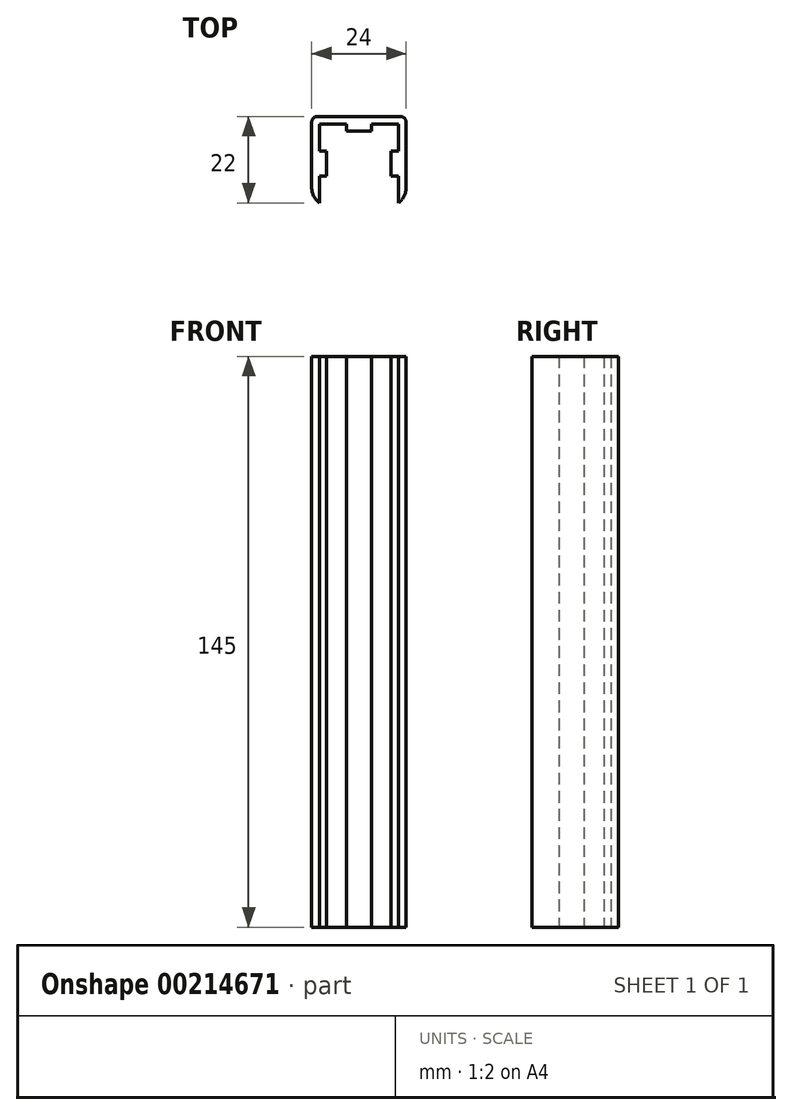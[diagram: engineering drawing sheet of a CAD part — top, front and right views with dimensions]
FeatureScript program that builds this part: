
annotation { "Feature Type Name" : "Feature", "Feature Type Description" : "" }
export const myFeature = defineFeature(function(context is Context, id is Id, definition is map)
    precondition{}
    {
        {
            var Q0;
            Q0=qCreatedBy(makeId("Top.planeOp"),FACE);
            var sketch = newSketch(context, id + "F0", { "sketchPlane" : qUnion([Q0])});
            skLineSegment(sketch, "E0", {"start": v(10.43, -32.44) * mm, "end": v(10.43, -25.64) * mm});
            skLineSegment(sketch, "E1", {"start": v(10.43, -25.64) * mm, "end": v(12.23, -25.64) * mm});
            skLineSegment(sketch, "E2", {"start": v(12.23, -25.64) * mm, "end": v(12.23, -19.24) * mm});
            skLineSegment(sketch, "E3", {"start": v(12.23, -19.24) * mm, "end": v(10.43, -19.24) * mm});
            skLineSegment(sketch, "E4", {"start": v(10.43, -19.24) * mm, "end": v(10.43, -12.44) * mm});
            skLineSegment(sketch, "E5", {"start": v(10.43, -12.44) * mm, "end": v(17.23, -12.44) * mm});
            skLineSegment(sketch, "E6", {"start": v(17.23, -12.44) * mm, "end": v(17.23, -14.24) * mm});
            skLineSegment(sketch, "E7", {"start": v(17.23, -14.24) * mm, "end": v(23.63, -14.24) * mm});
            skLineSegment(sketch, "E8", {"start": v(23.63, -14.24) * mm, "end": v(23.63, -12.44) * mm});
            skLineSegment(sketch, "E9", {"start": v(23.63, -12.44) * mm, "end": v(30.43, -12.44) * mm});
            skLineSegment(sketch, "E10", {"start": v(30.43, -12.44) * mm, "end": v(30.43, -19.24) * mm});
            skLineSegment(sketch, "E11", {"start": v(30.43, -19.24) * mm, "end": v(28.63, -19.24) * mm});
            skLineSegment(sketch, "E12", {"start": v(28.63, -19.24) * mm, "end": v(28.63, -25.64) * mm});
            skLineSegment(sketch, "E13", {"start": v(28.63, -25.64) * mm, "end": v(30.43, -25.64) * mm});
            skLineSegment(sketch, "E14", {"start": v(30.43, -25.64) * mm, "end": v(30.43, -32.44) * mm});
            skLineSegment(sketch, "E15", {"start": v(30.43, -32.44) * mm, "end": v(32.43, -32.44) * mm});
            skLineSegment(sketch, "E16", {"start": v(32.43, -32.44) * mm, "end": v(32.43, -10.44) * mm});
            skLineSegment(sketch, "E17", {"start": v(32.43, -10.44) * mm, "end": v(8.43, -10.44) * mm});
            skLineSegment(sketch, "E18", {"start": v(8.43, -10.44) * mm, "end": v(8.43, -32.44) * mm});
            skLineSegment(sketch, "E19", {"start": v(8.43, -32.44) * mm, "end": v(10.43, -32.44) * mm});
            skSolve(sketch);
        }
        {
            var Q0;
            Q0 = qSketchRegion(id + "F0", true);
            extrude(context, id + "F1", {"entities" : qUnion([Q0]), "offsetDistance" : 25 * mm, "depth" : 145 * mm});
        }
        {
            var Q0;
            Q0=makeQuery(id+"F1.opExtrude","SWEPT_EDGE",EDGE,{"disambiguationData":[OSD([sQuery(id+"F0.wireOp",EDGE,"E18"),sQuery(id+"F0.wireOp",EDGE,"E19")])]});
            var Q1;
            Q1=makeQuery(id+"F1.opExtrude","SWEPT_EDGE",EDGE,{"disambiguationData":[OSD([sQuery(id+"F0.wireOp",EDGE,"E15"),sQuery(id+"F0.wireOp",EDGE,"E16")])]});
            fillet(context, id + "F2", {"entities" : qUnion([Q0, Q1]), "radius" : 5 * mm, "tangentPropagation" : true, "allowEdgeOverflow" : false});
        }
        {
            var Q0;
            Q0=makeQuery(id+"F1.opExtrude","SWEPT_EDGE",EDGE,{"disambiguationData":[OSD([sQuery(id+"F0.wireOp",EDGE,"E17"),sQuery(id+"F0.wireOp",EDGE,"E18")])]});
            var Q1;
            Q1=makeQuery(id+"F1.opExtrude","SWEPT_EDGE",EDGE,{"disambiguationData":[OSD([sQuery(id+"F0.wireOp",EDGE,"E16"),sQuery(id+"F0.wireOp",EDGE,"E17")])]});
            fillet(context, id + "F3", {"entities" : qUnion([Q0, Q1]), "radius" : 1.5 * mm, "tangentPropagation" : true, "allowEdgeOverflow" : false});
        }
    });
